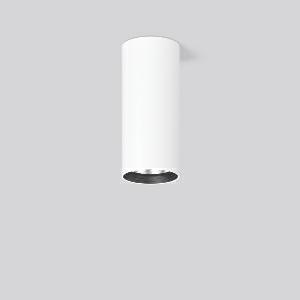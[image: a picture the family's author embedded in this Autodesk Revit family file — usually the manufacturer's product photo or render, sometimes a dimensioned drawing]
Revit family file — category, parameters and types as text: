
# Revit family: heledon_mini_a_931202_002_de76
name_source: partatom
category: Lighting Fixtures
units: mm (PartAtom-declared; Revit-internal decimal feet)

## family parameters
Cut with Voids When Loaded = No
Host = Face
Light Source = No
Part Type = Normal
Room Calculation Point = No
Round Connector Dimension = Use Diameter
Shared = No

## types (1)
- HELEDON mini A (1 x LED Modul 930, 2550 lm, 3000)
    Apparent Load = 20 VA
    Approval mark = CE
    CIE Flux Codes = 95 99 100 100 100
    Color Rendering = 90
    Color Temperature = 3000
    Default Elevation = 1800 mm
    Description = Series: HELEDON mini
Cylindrical surface-mounted downlight. Housing: die-cast aluminium, powder-coated. Internal ceiling frame polycarbonate with bayonet mounting. Black plastic ring and recessed LED to prevent glare from the side. Optical assembly with reflector made of MIRO-Silver with 98% total light reflection for outstanding efficiency - can be changed without tools. Best colour rendering index Ra>90. Suitable for Ceiling mounting. Easy installation with a separate ceiling frame with bayonet mounting and plug connection. Driver integrated. Connected via plug-in connector. High quality converter without flickering and stroboscopic effect. The following accessories can be mounted without use of tools: interchangeable lenses, decorative glasses, honeycomb louvre, clear and frosted diffusers, white interchangeable plastic ring. 
Colour: traffic white, matt (RAL 9016)
Diameter: 87 mm
Height: 197 mm
Lamp: LED
Socket: without socket
Colour temperature: 3000K
Colour rendering index (CRI): 92
System power: 20 W
Rated luminous flux: 2550 lm
Luminous efficiency: 128 lm/W
Control gear: Regulated power supply
Protection class: I
Type of protection: IP 20
    Height = 197 mm
    Lamp = 1 x LED Modul 930
    Lamp Light Flux = 2550 lm
    Lamp count = 1
    Length = 87 mm
    Lifetime = 50000 h
    Luminous efficacy = 128 lm/W
    Manufacturer = RZB
    ModVariant = No
    Model = 931202.002
    Mounting Place = Ceiling
    Mounting Type = Surface mounted
    Number of Poles = 1
    OnlyDefault = Yes
    Power Factor = 1
    Product Name = HELEDON mini A
    Product group = Surface mounted downlights
    ProductGroupID = 302
    Protection Class = Protection class I
    Protection Degree = IP 20
    RLX_Detail_Level = 1
    RLX_Emergency_Light_Flux = 0 lm
    RLX_Emergency_Type = 0
    RLX_Emergency_Type_DB = No
    RlxData = <blob elided: 104341 chars, md5=21921985>
    Socket = socket
    Standby Power = 0 W
    System Light Flux = 2550 lm
    System Power = 20 W
    Type Comments = Product without accessories
    Type Image = 931188.002.jpg
    URL = http://relux.com
    VarID = ---
    Voltage = 230 V
    Voltage Range = 220-240 V
    Weight = 0.00 kg
    Width = 0 mm  [stored 0 ft]

note: [stored X ft] marks values corroborated as IEEE doubles in the binary element streams (Revit-internal decimal feet)

## geometry (parser evidence)
native form markers: Blend x4, Sweep x10
no freeform markers — native parametric forms only
